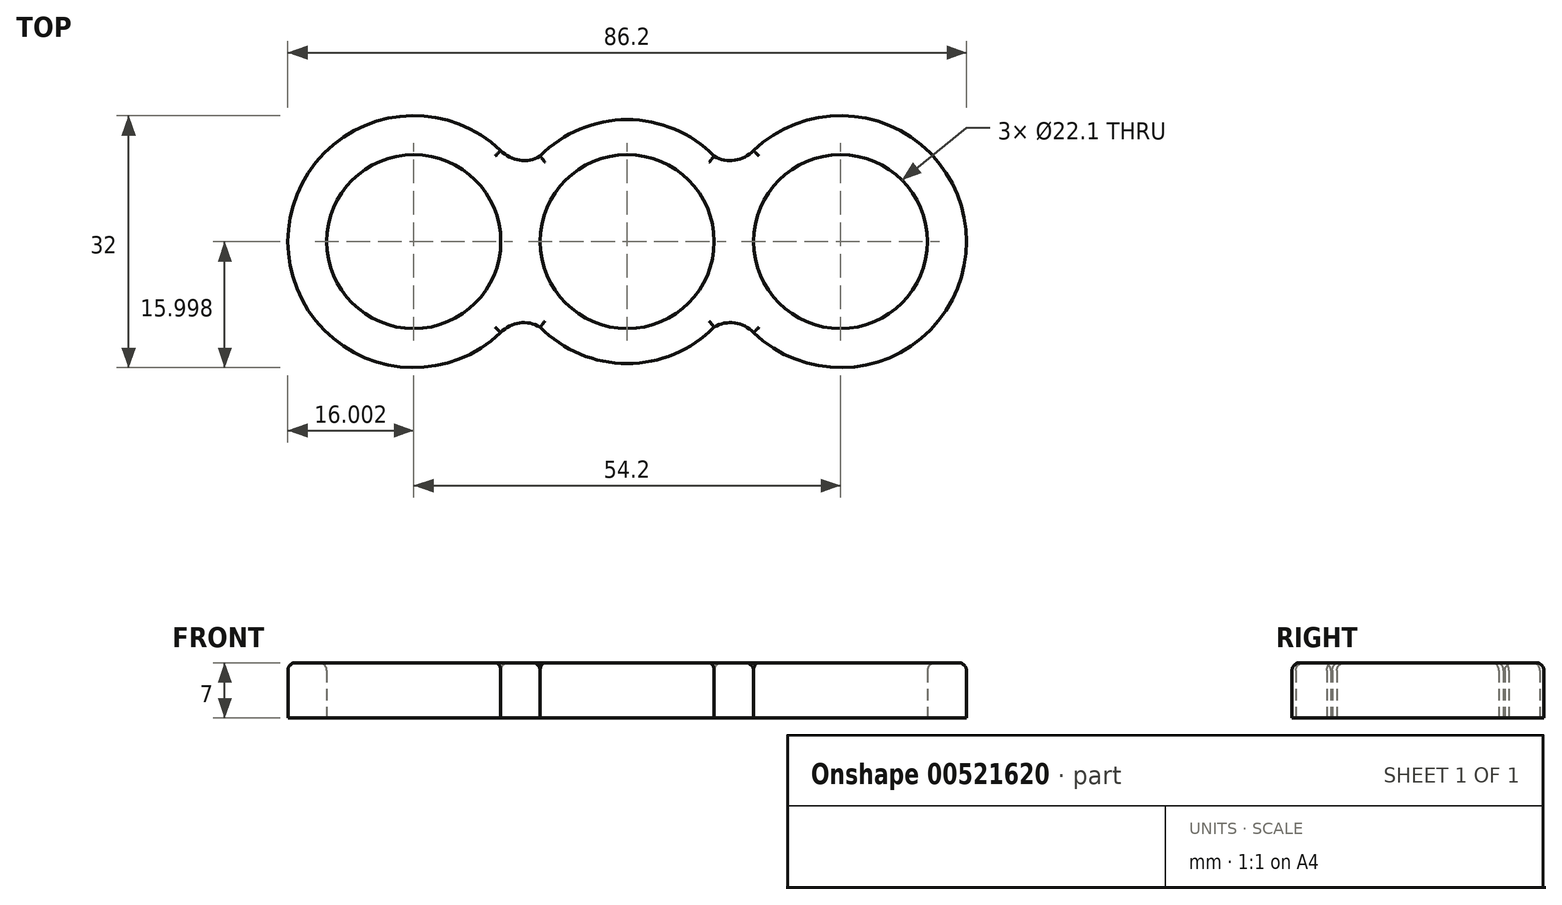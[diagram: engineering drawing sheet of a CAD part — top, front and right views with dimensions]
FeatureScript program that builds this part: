
annotation { "Feature Type Name" : "Feature", "Feature Type Description" : "" }
export const myFeature = defineFeature(function(context is Context, id is Id, definition is map)
    precondition{}
    {
        {
            var Q0;
            Q0=qCreatedBy(makeId("Top.planeOp"),FACE);
            var sketch = newSketch(context, id + "F0", { "sketchPlane" : qUnion([Q0])});
            skCircle(sketch, "E0", {"center": v(-8.18, 3.3) * mm, "radius": 11.05 * mm});
            skCircle(sketch, "E1", {"center": v(-35.28, 3.3) * mm, "radius": 11.05 * mm});
            skCircle(sketch, "E2", {"center": v(18.92, 3.3) * mm, "radius": 11.05 * mm});
            skCircle(sketch, "E3", {"center": v(-35.28, 3.3) * mm, "radius": 16 * mm});
            skCircle(sketch, "E4", {"center": v(-8.18, 3.3) * mm, "radius": 15.5 * mm});
            skCircle(sketch, "E5", {"center": v(18.92, 3.3) * mm, "radius": 16 * mm});
            skArc(sketch, "E6", {"start": v(-19.23, -7.57) * mm, "mid": v(-21.85, -7.03) * mm, "end": v(-24.23, -8.27) * mm});
            skPoint(sketch, "E6.startSnap0", {"position": v(-19.23, -4.4) * mm});
            skArc(sketch, "E7", {"start": v(7.87, -8.27) * mm, "mid": v(5.5, -7.03) * mm, "end": v(2.87, -7.57) * mm});
            skArc(sketch, "E8", {"start": v(2.87, 14.17) * mm, "mid": v(5.5, 13.63) * mm, "end": v(7.87, 14.87) * mm});
            skArc(sketch, "E9", {"start": v(-24.23, 14.87) * mm, "mid": v(-21.85, 13.63) * mm, "end": v(-19.23, 14.17) * mm});
            skSolve(sketch);
        }
        {
            var Q0;
            Q0=makeQuery(id+"F0.imprint","IMPRINT",FACE,{"disambiguationData":[TD([[makeQuery(id+"F0.imprint","IMPRINT",EDGE,{"derivedFrom":sQuery(id+"F0.wireOp",EDGE,"E0")}),-1.0]])]});
            var Q1;
            Q1=makeQuery(id+"F0.imprint","IMPRINT",FACE,{"disambiguationData":[TD([[makeQuery(id+"F0.imprint","IMPRINT",EDGE,{"derivedFrom":sQuery(id+"F0.wireOp",EDGE,"E1")}),-1.0]])]});
            var Q2;
            Q2=makeQuery(id+"F0.imprint","IMPRINT",FACE,{"disambiguationData":[TD([[makeQuery(id+"F0.imprint","IMPRINT",EDGE,{"derivedFrom":sQuery(id+"F0.wireOp",EDGE,"E2")}),-1.0]])]});
            var Q3;
            {var subQ0=sQuery(id+"F0.wireOp",EDGE,"E5");var subQ1=sQuery(id+"F0.wireOp",EDGE,"E4");var subQ2=makeQuery(id+"F0.imprint","INTERSECT",VERTEX,{"disambiguationData":[OD(0.0)],"derivedFrom":[subQ1,subQ0]});Q3=makeQuery(id+"F0.imprint","IMPRINT",FACE,{"disambiguationData":[TD([[makeQuery(id+"F0.imprint","IMPRINT",EDGE,{"disambiguationData":[TD([[subQ2,1.0]])],"derivedFrom":subQ1}),1.0]])]});}
            var Q4;
            {var subQ0=sQuery(id+"F0.wireOp",EDGE,"E4");var subQ1=sQuery(id+"F0.wireOp",EDGE,"E3");var subQ2=makeQuery(id+"F0.imprint","INTERSECT",VERTEX,{"disambiguationData":[OD(0.0)],"derivedFrom":[subQ1,subQ0]});Q4=makeQuery(id+"F0.imprint","IMPRINT",FACE,{"disambiguationData":[TD([[makeQuery(id+"F0.imprint","IMPRINT",EDGE,{"disambiguationData":[TD([[subQ2,1.0]])],"derivedFrom":subQ1}),1.0]])]});}
            var Q5;
            {var subQ0=sQuery(id+"F0.wireOp",EDGE,"E6");var subQ1=sQuery(id+"F0.wireOp",EDGE,"E3");var subQ2=makeQuery(id+"F0.imprint","INTERSECT",VERTEX,{"disambiguationData":[OD(1.0)],"derivedFrom":[subQ1,subQ0]});Q5=makeQuery(id+"F0.imprint","IMPRINT",FACE,{"disambiguationData":[TD([[makeQuery(id+"F0.imprint","IMPRINT",EDGE,{"disambiguationData":[TD([[subQ2,-1.0]])],"derivedFrom":subQ1}),-1.0]])]});}
            var Q6;
            {var subQ0=sQuery(id+"F0.wireOp",EDGE,"E9");var subQ1=sQuery(id+"F0.wireOp",EDGE,"E3");var subQ2=makeQuery(id+"F0.imprint","INTERSECT",VERTEX,{"disambiguationData":[OD(1.0)],"derivedFrom":[subQ1,subQ0]});Q6=makeQuery(id+"F0.imprint","IMPRINT",FACE,{"disambiguationData":[TD([[makeQuery(id+"F0.imprint","IMPRINT",EDGE,{"disambiguationData":[TD([[subQ2,1.0]])],"derivedFrom":subQ1}),-1.0]])]});}
            var Q7;
            {var subQ0=sQuery(id+"F0.wireOp",EDGE,"E8");var subQ1=sQuery(id+"F0.wireOp",EDGE,"E4");var subQ2=makeQuery(id+"F0.imprint","INTERSECT",VERTEX,{"derivedFrom":[subQ1,subQ0]});Q7=makeQuery(id+"F0.imprint","IMPRINT",FACE,{"disambiguationData":[TD([[makeQuery(id+"F0.imprint","IMPRINT",EDGE,{"disambiguationData":[TD([[subQ2,1.0]])],"derivedFrom":subQ1}),-1.0]])]});}
            var Q8;
            {var subQ0=sQuery(id+"F0.wireOp",EDGE,"E7");var subQ1=sQuery(id+"F0.wireOp",EDGE,"E4");var subQ2=makeQuery(id+"F0.imprint","INTERSECT",VERTEX,{"derivedFrom":[subQ1,subQ0]});Q8=makeQuery(id+"F0.imprint","IMPRINT",FACE,{"disambiguationData":[TD([[makeQuery(id+"F0.imprint","IMPRINT",EDGE,{"disambiguationData":[TD([[subQ2,-1.0]])],"derivedFrom":subQ1}),-1.0]])]});}
            extrude(context, id + "F1", {"entities" : qUnion([Q0, Q1, Q2, Q3, Q4, Q5, Q6, Q7, Q8]), "depth" : 7 * mm, "offsetDistance" : 25 * mm});
        }
        {
            var Q0;
            Q0=makeQuery(id+"F1.opExtrude","CAP_FACE",FACE,{"disambiguationData":[OSD([sQuery(id+"F0.wireOp",EDGE,"E0"),sQuery(id+"F0.wireOp",EDGE,"E1"),sQuery(id+"F0.wireOp",EDGE,"E2"),sQuery(id+"F0.wireOp",EDGE,"E3"),sQuery(id+"F0.wireOp",EDGE,"E4"),sQuery(id+"F0.wireOp",EDGE,"E5"),sQuery(id+"F0.wireOp",EDGE,"E6"),sQuery(id+"F0.wireOp",EDGE,"E7"),sQuery(id+"F0.wireOp",EDGE,"E8"),sQuery(id+"F0.wireOp",EDGE,"E9")])],"isStart":false});
            fillet(context, id + "F2", {"entities" : qUnion([Q0]), "radius" : 1 * mm, "tangentPropagation" : true, "allowEdgeOverflow" : false});
        }
    });
